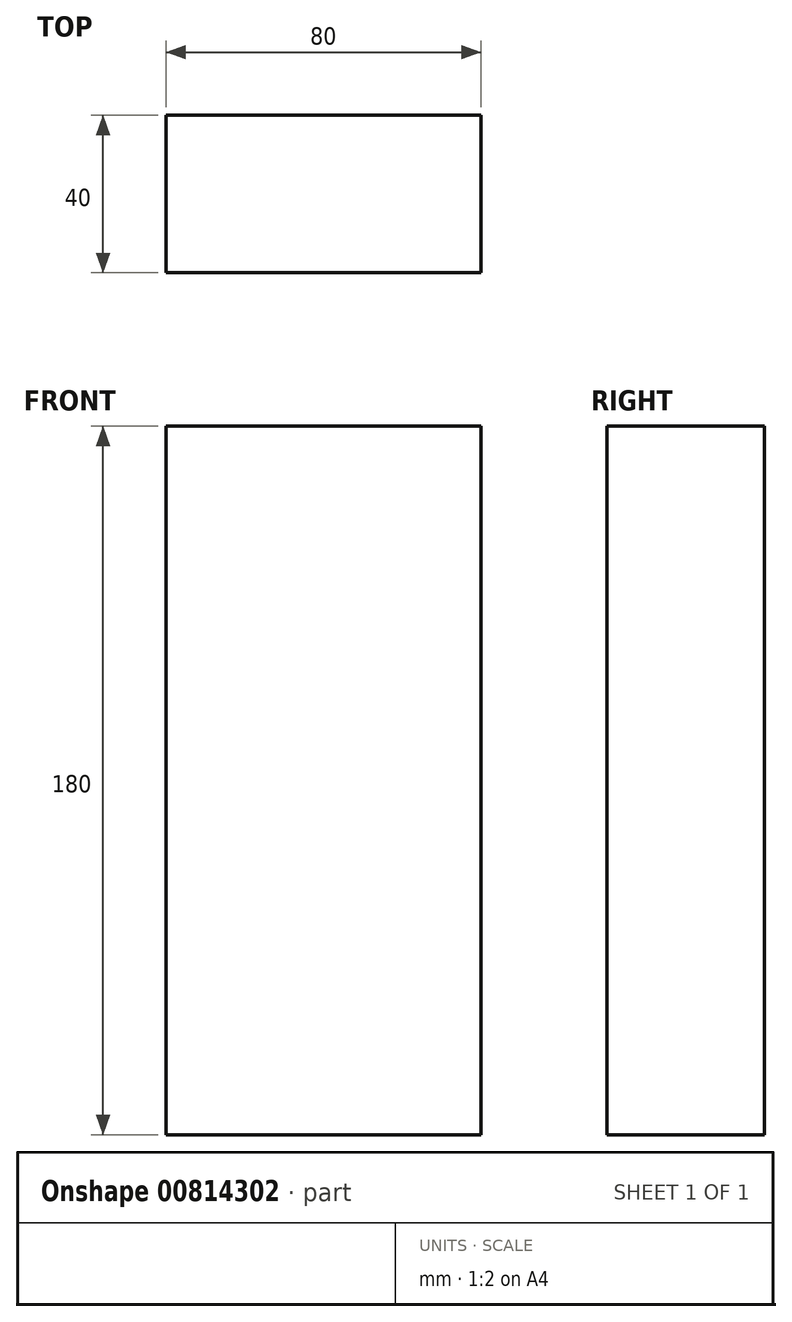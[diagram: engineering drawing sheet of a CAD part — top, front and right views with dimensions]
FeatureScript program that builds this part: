
annotation { "Feature Type Name" : "Feature", "Feature Type Description" : "" }
export const myFeature = defineFeature(function(context is Context, id is Id, definition is map)
    precondition{}
    {
        {
            var Q0;
            Q0=qCreatedBy(makeId("Top.planeOp"),FACE);
            var sketch = newSketch(context, id + "F0", { "sketchPlane" : qUnion([Q0])});
            skLineSegment(sketch, "E0.bottom", {"start": v(40, 20) * mm, "end": v(-40, 20) * mm});
            skLineSegment(sketch, "E0.top", {"start": v(40, -20) * mm, "end": v(-40, -20) * mm});
            skLineSegment(sketch, "E0.left", {"start": v(40, 20) * mm, "end": v(40, -20) * mm});
            skLineSegment(sketch, "E0.right", {"start": v(-40, 20) * mm, "end": v(-40, -20) * mm});
            skPoint(sketch, "E0.middle", {"position": v(0, 0) * mm});
            skSolve(sketch);
        }
        {
            var Q0;
            Q0=makeQuery(id+"F0.imprint","IMPRINT",FACE,{"disambiguationData":[TD([[makeQuery(id+"F0.imprint","IMPRINT",EDGE,{"derivedFrom":sQuery(id+"F0.wireOp",EDGE,"E0.bottom")}),1.0]])]});
            extrude(context, id + "F1", {"entities" : qUnion([Q0]), "depth" : 90 * mm, "offsetDistance" : 25 * mm, "hasSecondDirection" : true, "secondDirectionOppositeDirection" : true, "secondDirectionDepth" : 90 * mm});
        }
    });
